SOLIDWORKS PART (.sldprt)
format: sldprt  version: not decoded by parser v0  size: 116,736 bytes
history: native  units: mm
features: plane x5, sketch x5, extrude x3, material x1, cut_extrude x1, cut_revolve x1 (+12 scaffold rows collapsed)
feature tree (28):
  scaffold x12  (default folders/planes/origin — collapsed)
  material  "Material <not specified>"
  plane  "Plane1"
  sketch  "Sketch1"
  extrude  "Boss-Extrude1"  Depth=4mm
  plane  "Plane2"
  sketch  "Sketch2"
  extrude  "Boss-Extrude2"  Depth=1.5mm
  plane  "Plane3"
  sketch  "Sketch3"
  extrude  "Boss-Extrude3"  Depth=1.5mm
  plane  "Plane4"
  sketch  "Sketch4"
  cut_extrude  "Cut-Extrude1"  Depth=4mm
  plane  "Plane5"
  sketch  "Sketch5"
  cut_revolve  "Cut-Revolve1"  Angle=360deg
decode coverage: 5 of 10 modeling features carry decoded parameters
note: suppression state not decoded; provenance and decode notes live in map.json
